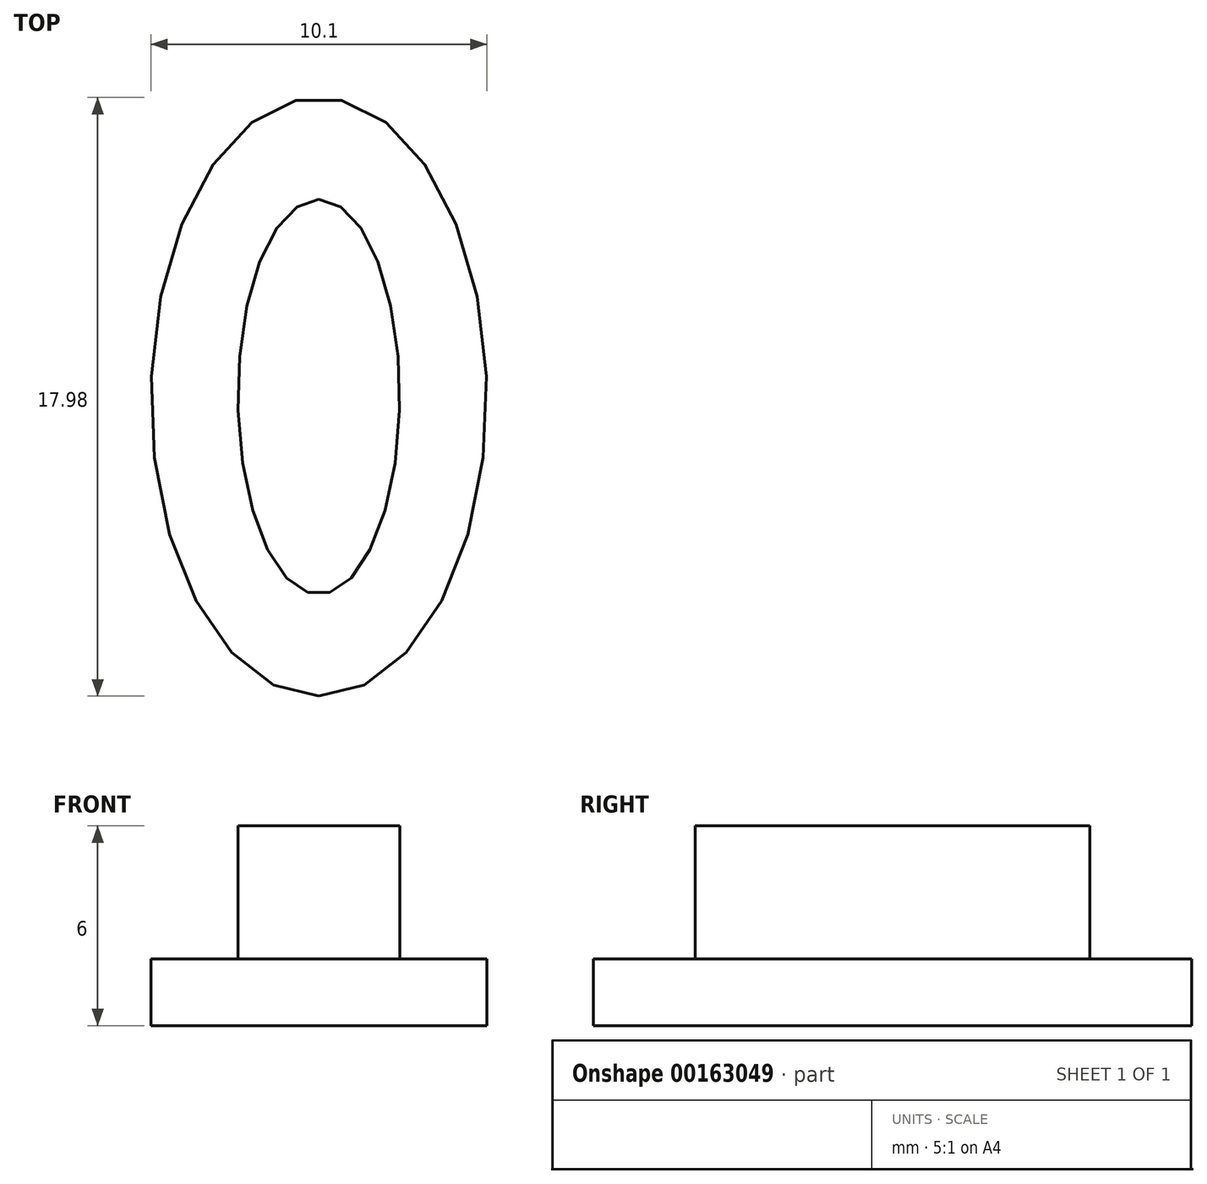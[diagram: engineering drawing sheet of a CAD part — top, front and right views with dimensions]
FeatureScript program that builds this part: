
annotation { "Feature Type Name" : "Feature", "Feature Type Description" : "" }
export const myFeature = defineFeature(function(context is Context, id is Id, definition is map)
    precondition{}
    {
        {
            var Q0;
            Q0=qCreatedBy(makeId("Top.planeOp"),FACE);
            var sketch = newSketch(context, id + "F0", { "sketchPlane" : qUnion([Q0])});
            skPoint(sketch, "E0.middle", {"position": v(0, 0) * mm});
            skEllipse(sketch, "E1", {"center": v(0, 0) * mm, "majorRadius": 5.93 * mm, "minorRadius": 2.43 * mm, "majorAxis": v(0, 1)});
            skSolve(sketch);
        }
        {
            var Q0;
            Q0=makeQuery(id+"F0.imprint","IMPRINT",FACE,{"disambiguationData":[TD([[makeQuery(id+"F0.imprint","IMPRINT",EDGE,{"derivedFrom":sQuery(id+"F0.wireOp",EDGE,"E1")}),1.0]])]});
            extrude(context, id + "F1", {"entities" : qUnion([Q0]), "depth" : 4 * mm});
        }
        {
            var Q0;
            Q0=qCreatedBy(makeId("Top.planeOp"),FACE);
            var sketch = newSketch(context, id + "F2", { "sketchPlane" : qUnion([Q0])});
            skEllipse(sketch, "E2", {"center": v(0, 0) * mm, "majorRadius": 9 * mm, "minorRadius": 5.05 * mm, "majorAxis": v(0, -1)});
            skSolve(sketch);
        }
        {
            var Q0;
            Q0 = qSketchRegion(id + "F2", true);
            extrude(context, id + "F3", {"entities" : qUnion([Q0]), "oppositeDirection" : true, "depth" : 2 * mm});
        }
    });
